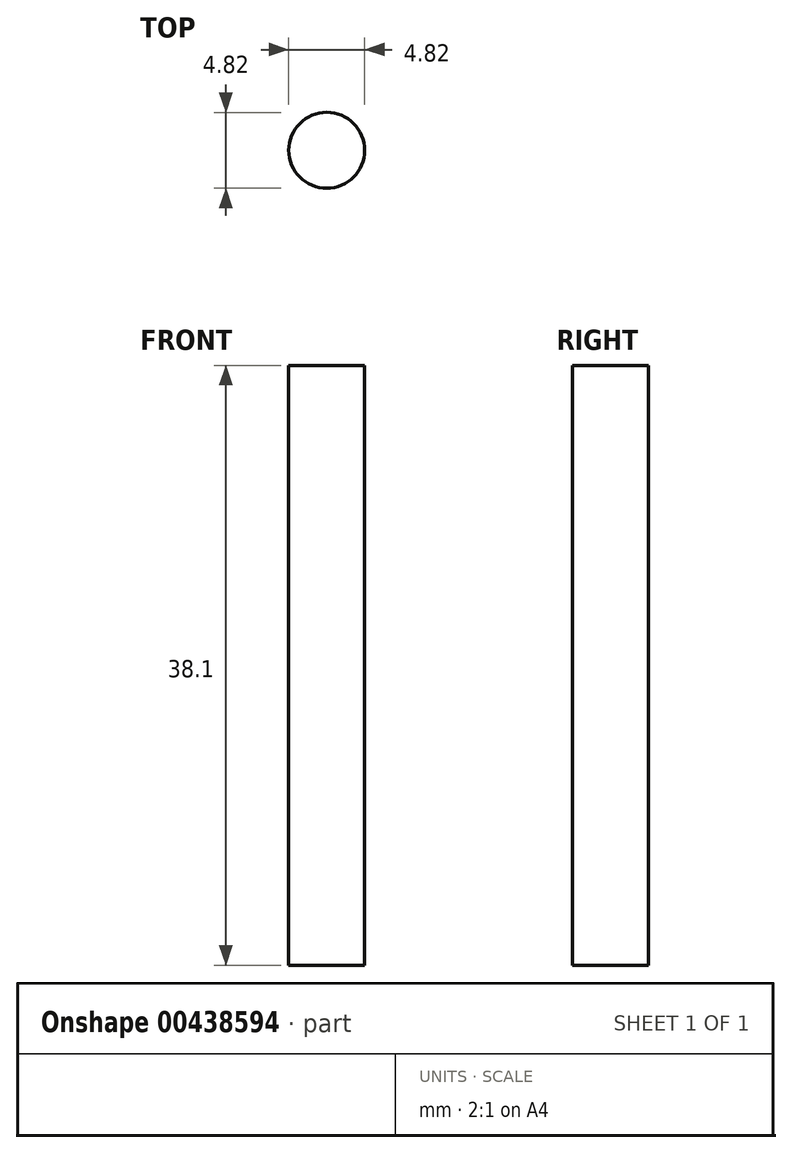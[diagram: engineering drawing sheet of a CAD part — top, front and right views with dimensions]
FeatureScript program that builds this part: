
annotation { "Feature Type Name" : "Feature", "Feature Type Description" : "" }
export const myFeature = defineFeature(function(context is Context, id is Id, definition is map)
    precondition{}
    {
        {
            var Q0;
            Q0=qCreatedBy(makeId("Top.planeOp"),FACE);
            var sketch = newSketch(context, id + "F0", { "sketchPlane" : qUnion([Q0])});
            skCircle(sketch, "E0", {"center": v(0, 0) * mm, "radius": 2.41 * mm});
            skSolve(sketch);
        }
        {
            var Q0;
            Q0 = qSketchRegion(id + "F0", true);
            extrude(context, id + "F1", {"entities" : qUnion([Q0]), "depth" : 38.1 * mm});
        }
    });
